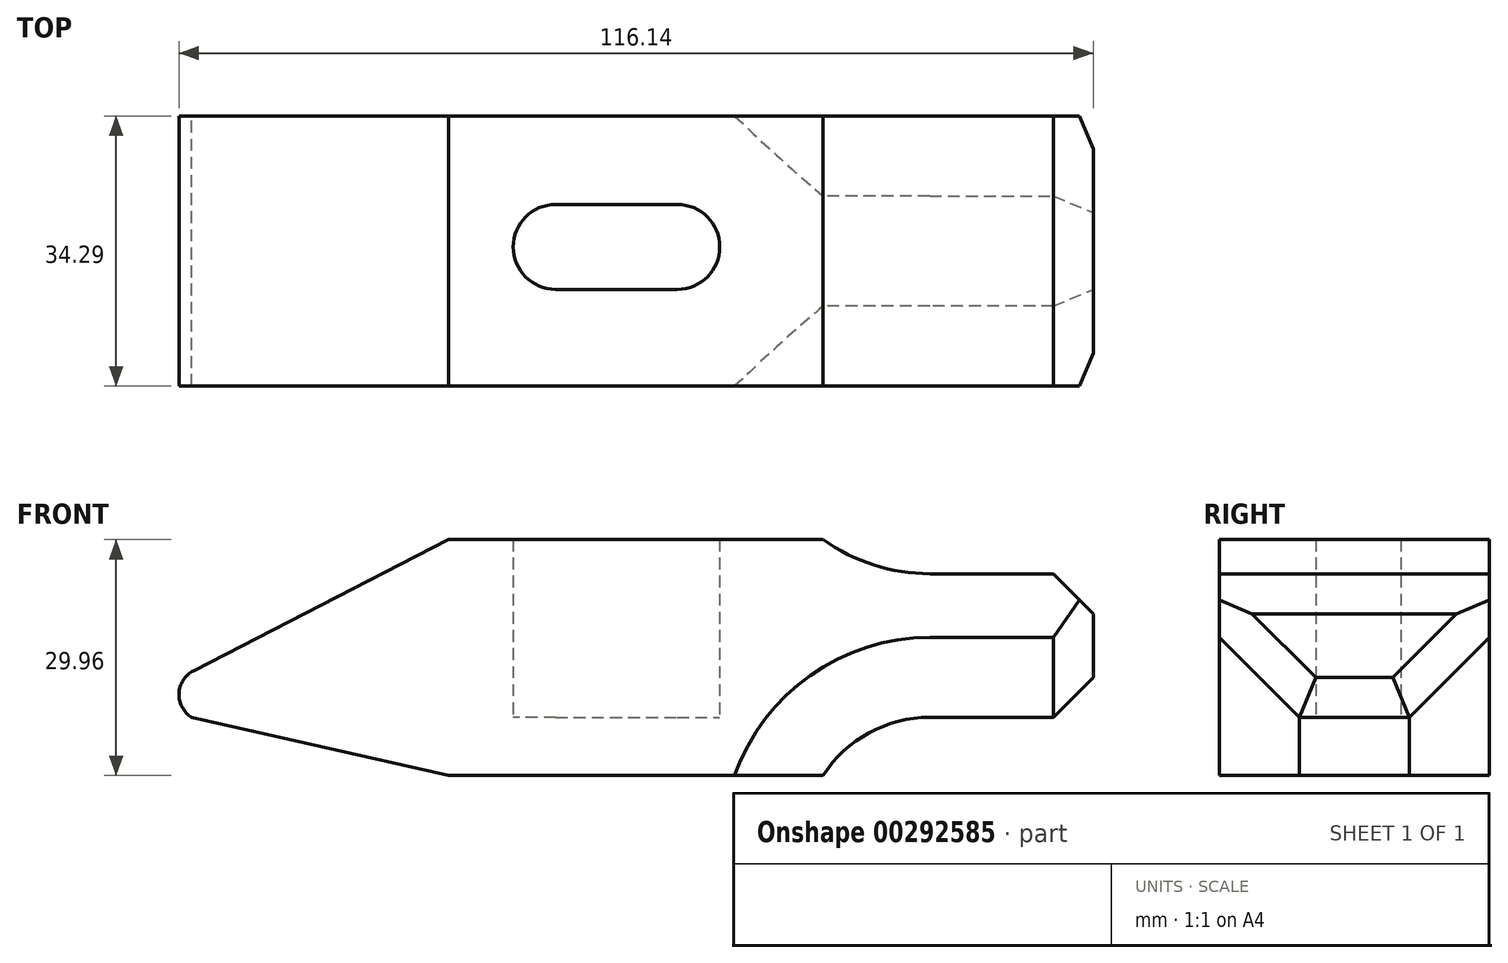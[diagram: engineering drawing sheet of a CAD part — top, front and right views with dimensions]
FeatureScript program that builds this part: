
annotation { "Feature Type Name" : "Feature", "Feature Type Description" : "" }
export const myFeature = defineFeature(function(context is Context, id is Id, definition is map)
    precondition{}
    {
        {
            var Q0;
            Q0=qCreatedBy(makeId("Front.planeOp"),FACE);
            var sketch = newSketch(context, id + "F0", { "sketchPlane" : qUnion([Q0])});
            skLineSegment(sketch, "E0", {"start": v(-24.4, 22.6) * mm, "end": v(23.2, 22.6) * mm});
            skLineSegment(sketch, "E1", {"start": v(23.2, -7.37) * mm, "end": v(-24.4, -7.37) * mm});
            skLineSegment(sketch, "E2", {"start": v(-24.4, 22.6) * mm, "end": v(-56.79, 5.92) * mm});
            skLineSegment(sketch, "E3", {"start": v(-24.4, -7.37) * mm, "end": v(-57.03, 0) * mm});
            skArc(sketch, "E4", {"start": v(-56.79, 5.92) * mm, "mid": v(-58.63, 3.03) * mm, "end": v(-57.03, 0) * mm});
            skLineSegment(sketch, "E5", {"start": v(57.51, 18.24) * mm, "end": v(36.73, 18.24) * mm});
            skLineSegment(sketch, "E6", {"start": v(36.73, 18.24) * mm, "end": v(57.51, 18.24) * mm});
            skLineSegment(sketch, "E7", {"start": v(57.51, 0) * mm, "end": v(36.73, 0) * mm});
            skArc(sketch, "E8", {"start": v(23.2, 22.6) * mm, "mid": v(29.62, 19.36) * mm, "end": v(36.73, 18.24) * mm});
            skArc(sketch, "E9", {"start": v(36.73, 0) * mm, "mid": v(29.03, -1.96) * mm, "end": v(23.2, -7.37) * mm});
            skLineSegment(sketch, "E10", {"start": v(57.51, 18.24) * mm, "end": v(57.51, 0) * mm});
            skSolve(sketch);
        }
        {
            var Q0;
            Q0 = qSketchRegion(id + "F0", true);
            extrude(context, id + "F1", {"entities" : qUnion([Q0]), "depth" : 34.3 * mm});
        }
        {
            var Q0;
            Q0=makeQuery(id+"F1.opExtrude","CAP_EDGE",EDGE,{"disambiguationData":[OSD([sQuery(id+"F0.wireOp",EDGE,"E6")])],"isStart":false});
            var Q1;
            Q1=makeQuery(id+"F1.opExtrude","CAP_EDGE",EDGE,{"disambiguationData":[OSD([sQuery(id+"F0.wireOp",EDGE,"E7")])],"isStart":false});
            var Q2;
            Q2=makeQuery(id+"F1.opExtrude","CAP_EDGE",EDGE,{"disambiguationData":[OSD([sQuery(id+"F0.wireOp",EDGE,"E7")])],"isStart":true});
            var Q3;
            Q3=makeQuery(id+"F1.opExtrude","CAP_EDGE",EDGE,{"disambiguationData":[OSD([sQuery(id+"F0.wireOp",EDGE,"E6")])],"isStart":true});
            chamfer(context, id + "F2", {"entities" : qUnion([Q0, Q1, Q2, Q3]), "width" : 10.16 * mm, "tangentPropagation" : true});
        }
        {
            var Q0;
            Q0=qCreatedBy(makeId("Top.planeOp"),FACE);
            var sketch = newSketch(context, id + "F3", { "sketchPlane" : qUnion([Q0])});
            skLineSegment(sketch, "E11", {"start": v(-10.78, -11.22) * mm, "end": v(4.66, -11.22) * mm});
            skLineSegment(sketch, "E12", {"start": v(4.66, -22) * mm, "end": v(-10.78, -22) * mm});
            skArc(sketch, "E13", {"start": v(-10.78, -11.22) * mm, "mid": v(-16.18, -16.61) * mm, "end": v(-10.78, -22) * mm});
            skArc(sketch, "E14", {"start": v(4.66, -22) * mm, "mid": v(10.06, -16.61) * mm, "end": v(4.66, -11.22) * mm});
            skSolve(sketch);
        }
        {
            var Q0;
            Q0 = qSketchRegion(id + "F3", true);
            extrude(context, id + "F4", {"entities" : qUnion([Q0]), "operationType" : NewBodyOperationType.REMOVE, "depth" : 64 * mm});
        }
        {
            var Q0;
            Q0=makeQuery(id+"F2.opChamfer","BLEND_EDGE",EDGE,{"blendedFrom":[makeQuery(id+"F1.opExtrude","CAP_EDGE",EDGE,{"disambiguationData":[OSD([sQuery(id+"F0.wireOp",EDGE,"E6")])],"isStart":false}),makeQuery(id+"F1.opExtrude","SWEPT_FACE",FACE,{"disambiguationData":[OSD([sQuery(id+"F0.wireOp",EDGE,"E10")])]})],"blendedInto":[makeQuery(id+"F1.opExtrude","SWEPT_FACE",FACE,{"disambiguationData":[OSD([sQuery(id+"F0.wireOp",EDGE,"E10")])]})]});
            var Q1;
            Q1=makeQuery(id+"F1.opExtrude","SWEPT_EDGE",EDGE,{"disambiguationData":[OSD([sQuery(id+"F0.wireOp",EDGE,"E6"),sQuery(id+"F0.wireOp",EDGE,"E10")])]});
            var Q2;
            Q2=makeQuery(id+"F2.opChamfer","BLEND_EDGE",EDGE,{"blendedFrom":[makeQuery(id+"F1.opExtrude","CAP_EDGE",EDGE,{"disambiguationData":[OSD([sQuery(id+"F0.wireOp",EDGE,"E6")])],"isStart":true}),makeQuery(id+"F1.opExtrude","SWEPT_FACE",FACE,{"disambiguationData":[OSD([sQuery(id+"F0.wireOp",EDGE,"E10")])]})],"blendedInto":[makeQuery(id+"F1.opExtrude","SWEPT_FACE",FACE,{"disambiguationData":[OSD([sQuery(id+"F0.wireOp",EDGE,"E10")])]})]});
            var Q3;
            Q3=makeQuery(id+"F1.opExtrude","SWEPT_EDGE",EDGE,{"disambiguationData":[OSD([sQuery(id+"F0.wireOp",EDGE,"E7"),sQuery(id+"F0.wireOp",EDGE,"E10")])]});
            var Q4;
            Q4=makeQuery(id+"F2.opChamfer","BLEND_EDGE",EDGE,{"blendedFrom":[makeQuery(id+"F1.opExtrude","CAP_EDGE",EDGE,{"disambiguationData":[OSD([sQuery(id+"F0.wireOp",EDGE,"E7")])],"isStart":false}),makeQuery(id+"F1.opExtrude","SWEPT_FACE",FACE,{"disambiguationData":[OSD([sQuery(id+"F0.wireOp",EDGE,"E10")])]})],"blendedInto":[makeQuery(id+"F1.opExtrude","SWEPT_FACE",FACE,{"disambiguationData":[OSD([sQuery(id+"F0.wireOp",EDGE,"E10")])]})]});
            var Q5;
            Q5=makeQuery(id+"F2.opChamfer","BLEND_EDGE",EDGE,{"blendedFrom":[makeQuery(id+"F1.opExtrude","CAP_EDGE",EDGE,{"disambiguationData":[OSD([sQuery(id+"F0.wireOp",EDGE,"E7")])],"isStart":true}),makeQuery(id+"F1.opExtrude","SWEPT_FACE",FACE,{"disambiguationData":[OSD([sQuery(id+"F0.wireOp",EDGE,"E10")])]})],"blendedInto":[makeQuery(id+"F1.opExtrude","SWEPT_FACE",FACE,{"disambiguationData":[OSD([sQuery(id+"F0.wireOp",EDGE,"E10")])]})]});
            chamfer(context, id + "F5", {"entities" : qUnion([Q0, Q1, Q2, Q3, Q4, Q5]), "width" : 5.08 * mm, "tangentPropagation" : true});
        }
    });
